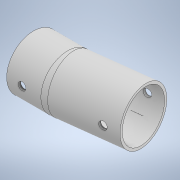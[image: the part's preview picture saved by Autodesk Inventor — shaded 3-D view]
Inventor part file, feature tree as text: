
AUTODESK INVENTOR PART (.ipt)
format: ipt  version: 2022 (Build 260153000, 153)  size: 246,784 bytes
history: native  units: mm
features: sketch x4, extrude x2, sweep x1
ambient origin geometry x8: Origin, YZ Plane, XZ Plane, XY Plane, X Axis, Y Axis, Z Axis, Center Point
bodies: Body1 (feature_tree)
feature tree (7):
  sweep  "Sweep1"
  extrude  "Extrusion8"  Depth=30.194196mm
  extrude  "Extrusion9"  Depth=10.0mm
  sketch  "Sketch5"  dims[d31=34.456mm d122=14.0mm]
  sketch  "Sketch6"  dims[d123=26.0mm d124=30.194196mm]
  sketch  "Sketch7"  dims[d125=10.0mm d126=19.0mm]
  sketch  "Sketch8"  dims[d127=21.0mm d128=0.0mm d129=0.0mm d130=6.0mm d131=3.0mm d132=25.0mm d133=0.0mm d134=6.0mm d135=3.0mm d136=25.0mm d137=0.0mm d138=0.01mm d139=0.01mm]
